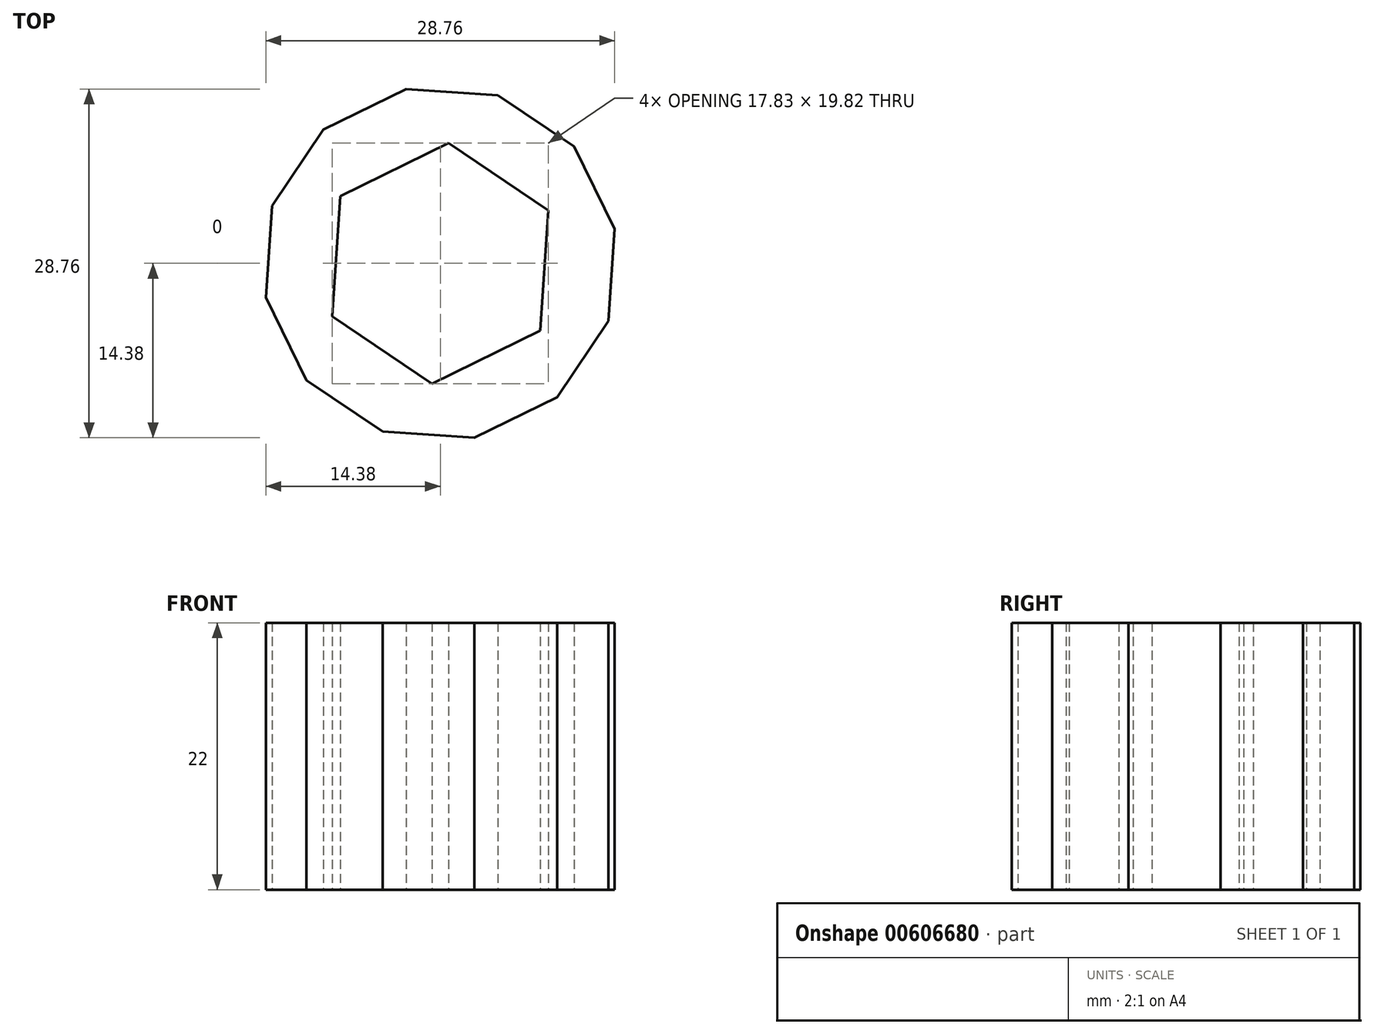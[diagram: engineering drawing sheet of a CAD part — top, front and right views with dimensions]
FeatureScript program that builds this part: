
annotation { "Feature Type Name" : "Feature", "Feature Type Description" : "" }
export const myFeature = defineFeature(function(context is Context, id is Id, definition is map)
    precondition{}
    {
        {
            var Q0;
            Q0=qCreatedBy(makeId("Top.planeOp"),FACE);
            var sketch = newSketch(context, id + "F0", { "sketchPlane" : qUnion([Q0])});
            skCircle(sketch, "E0", {"center": v(0, 0) * mm, "radius": 14.65 * mm});
            skCircle(sketch, "E1.cCircle", {"center": v(0, 0) * mm, "radius": 8.6 * mm, "construction": true});
            skLineSegment(sketch, "E1.0", {"start": v(0.67, 9.9) * mm, "end": v(8.92, 4.37) * mm});
            skLineSegment(sketch, "E1.1", {"start": v(8.92, 4.37) * mm, "end": v(8.24, -5.54) * mm});
            skLineSegment(sketch, "E1.2", {"start": v(8.24, -5.54) * mm, "end": v(-0.67, -9.9) * mm});
            skLineSegment(sketch, "E1.3", {"start": v(-0.67, -9.9) * mm, "end": v(-8.92, -4.37) * mm});
            skLineSegment(sketch, "E1.4", {"start": v(-8.92, -4.37) * mm, "end": v(-8.24, 5.54) * mm});
            skLineSegment(sketch, "E1.5", {"start": v(-8.24, 5.54) * mm, "end": v(0.67, 9.9) * mm});
            skPoint(sketch, "E1.0.midPoint", {"position": v(4.8, 7.14) * mm});
            skCircle(sketch, "E2.cCircle", {"center": v(0, 0) * mm, "radius": 14.65 * mm, "construction": true});
            skLineSegment(sketch, "E2.0", {"start": v(4.74, 13.86) * mm, "end": v(11.04, 9.63) * mm});
            skLineSegment(sketch, "E2.1", {"start": v(11.04, 9.63) * mm, "end": v(14.38, 2.82) * mm});
            skLineSegment(sketch, "E2.2", {"start": v(14.38, 2.82) * mm, "end": v(13.86, -4.74) * mm});
            skLineSegment(sketch, "E2.3", {"start": v(13.86, -4.74) * mm, "end": v(9.63, -11.04) * mm});
            skLineSegment(sketch, "E2.4", {"start": v(9.63, -11.04) * mm, "end": v(2.82, -14.38) * mm});
            skLineSegment(sketch, "E2.5", {"start": v(2.82, -14.38) * mm, "end": v(-4.74, -13.86) * mm});
            skLineSegment(sketch, "E2.6", {"start": v(-4.74, -13.86) * mm, "end": v(-11.04, -9.63) * mm});
            skLineSegment(sketch, "E2.7", {"start": v(-11.04, -9.63) * mm, "end": v(-14.38, -2.82) * mm});
            skLineSegment(sketch, "E2.8", {"start": v(-14.38, -2.82) * mm, "end": v(-13.86, 4.74) * mm});
            skLineSegment(sketch, "E2.9", {"start": v(-13.86, 4.74) * mm, "end": v(-9.63, 11.04) * mm});
            skLineSegment(sketch, "E2.10", {"start": v(-9.63, 11.04) * mm, "end": v(-2.82, 14.38) * mm});
            skLineSegment(sketch, "E2.11", {"start": v(-2.82, 14.38) * mm, "end": v(4.74, 13.86) * mm});
            skSolve(sketch);
        }
        {
            var Q0;
            Q0=makeQuery(id+"F0.imprint","IMPRINT",FACE,{"disambiguationData":[TD([[makeQuery(id+"F0.imprint","IMPRINT",EDGE,{"derivedFrom":sQuery(id+"F0.wireOp",EDGE,"E1.0")}),1.0]])]});
            extrude(context, id + "F1", {"entities" : qUnion([Q0]), "depth" : 22 * mm, "offsetDistance" : 25 * mm});
        }
    });
